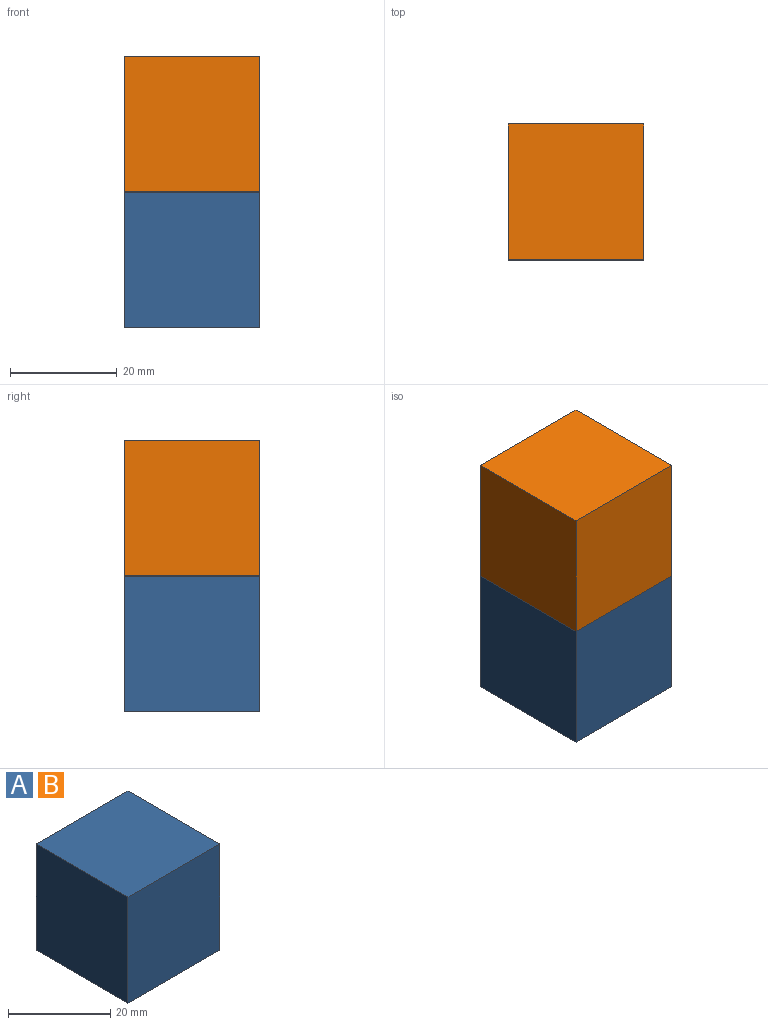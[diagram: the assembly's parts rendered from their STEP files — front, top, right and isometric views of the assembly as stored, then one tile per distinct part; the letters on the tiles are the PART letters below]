
ASSEMBLY  parts=2 mates=1
PART A: 6 faces, bbox 25.4x25.4x25.4 mm
  f0: plane 25.4x25.4mm, normal (-1,0,0), area 645.2mm2, adj f1,f3,f4,f5
  f1: plane 25.4x25.4mm, normal (0,0,-1), area 645.2mm2, adj f0,f2,f4,f5
  f2: plane 25.4x25.4mm, normal (1,0,0), area 645.2mm2, adj f1,f3,f4,f5
  f3: plane 25.4x25.4mm, normal (0,0,1), area 645.2mm2, adj f0,f2,f4,f5
  f4: plane 25.4x25.4mm, normal (0,-1,0), area 645.2mm2, adj f0,f1,f2,f3
  f5: plane 25.4x25.4mm, normal (0,1,0), area 645.2mm2, adj f0,f1,f2,f3
PART B: same geometry as A
PLACE A t=(-18.3,27.63,-19.39)mm
PLACE B t=(-18.3,27.63,6.01)mm
MATE fastened B.f1 <-> A.f3  axis (0,0,-1) through (16.46,14.93,20.85)mm
